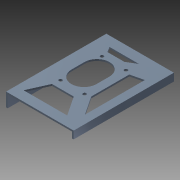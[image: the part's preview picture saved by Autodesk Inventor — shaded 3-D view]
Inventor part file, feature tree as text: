
AUTODESK INVENTOR PART (.ipt)
format: ipt  version: 2013 (Build 170138000, 138)  size: 159,744 bytes
history: native  units: mm
features: sketch x5, extrude x4, other x1, hole x1
ambient origin geometry x1: Origin
feature tree (11):
  other  "ソリッド1"
  extrude  "押し出し1"  Depth=92.0mm
  hole  "穴1"  [1 undecoded]
  extrude  "押し出し3"  Depth=62.0mm
  extrude  "押し出し5"  Depth=31.0mm
  extrude  "押し出し7"  Depth=1.5mm TaperAngle=0.0deg
  sketch  "スケッチ1"
  sketch  "スケッチ3"
  sketch  "スケッチ4"
  sketch  "スケッチ6"
  sketch  "スケッチ7"
note: 1 required parameter value undecoded (feature->parameter linkage not recoverable at this tier; creation-order binding heuristic only, values carry confidence <= 0.55)
